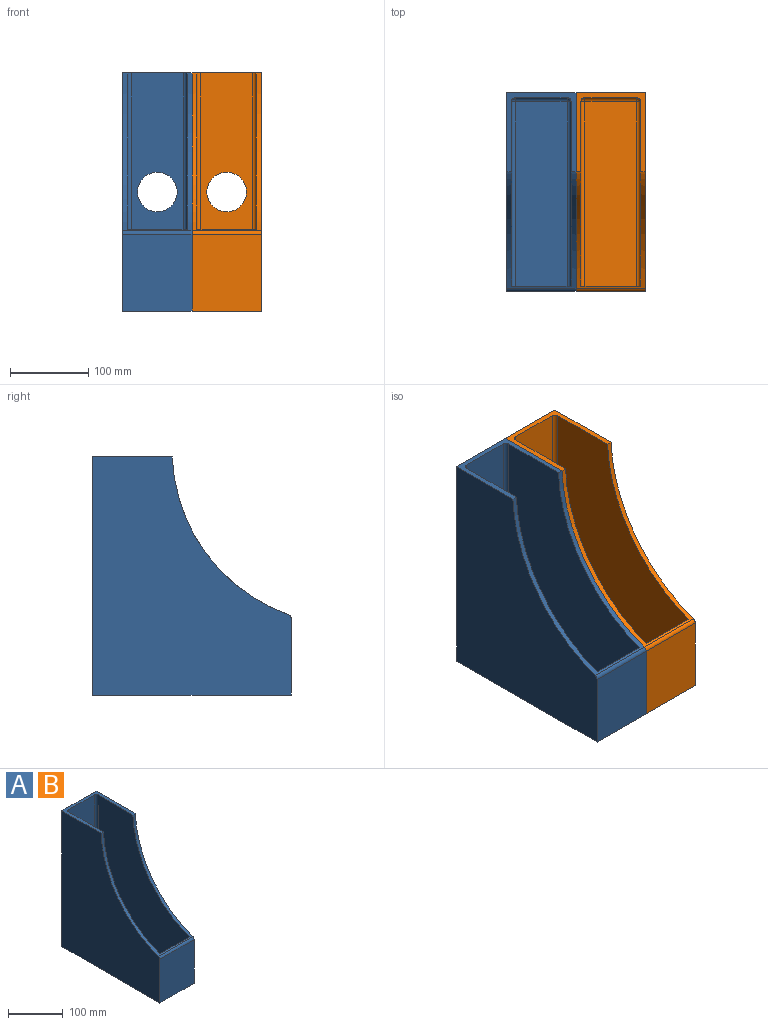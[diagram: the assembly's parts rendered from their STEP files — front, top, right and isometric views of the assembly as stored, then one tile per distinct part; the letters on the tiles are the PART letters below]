
ASSEMBLY  parts=2 mates=1
PART A: 21 faces, bbox 88.9x254x304.8 mm
  f0: cylinder r=224.76mm len=202.03mm, axis (-1,0,0), area 3624.3mm2, adj f4,f5,f6,f9,f10,f11,f19
  f1: plane 97.99x88.9mm, normal (0,-1,0), area 8711.2mm2, adj f2,f6,f11,f19
  f2: plane 254x88.9mm, normal (0,0,-1), area 22580.6mm2, adj f1,f3,f6,f11
  f3: plane 304.8x88.9mm, normal (0,1,0), area 25069.9mm2, adj f2,f4,f6,f11,f20
  f4: plane 101.6x88.9mm, normal (0,0,1), area 1785.3mm2, adj f0,f3,f5,f6,f7,f10,f11,f12
  f5: plane 293.37x236.22mm, normal (1,0,0), area 48315.3mm2, adj f0,f4,f9,f14,f15
  f6: plane 304.8x254mm, normal (-1,0,0), area 55149mm2, adj f0,f1,f2,f3,f4,f19
  f7: plane 293.37x66.04mm, normal (0,-1,0), area 17347.3mm2, adj f4,f12,f15,f18,f20
  f8: plane 236.22x66.04mm, normal (0,0,1), area 15600mm2, adj f9,f13,f14,f18
  f9: plane 97.51x76.2mm, normal (0,1,0), area 7419.1mm2, adj f0,f5,f8,f10,f13,f14
  f10: plane 293.37x236.22mm, normal (-1,0,0), area 48315.3mm2, adj f0,f4,f9,f12,f13
  f11: plane 304.8x254mm, normal (1,0,0), area 55149mm2, adj f0,f1,f2,f3,f4,f19
  f12: cylinder r=5.08mm len=293.37mm, axis (0,0,1), area 2341mm2, adj f4,f7,f10,f16
  f13: cylinder r=5.08mm len=236.22mm, axis (0,1,0), area 1885mm2, adj f8,f9,f10,f16
  f14: cylinder r=5.08mm len=236.22mm, axis (0,-1,0), area 1885mm2, adj f5,f8,f9,f17
  f15: cylinder r=5.08mm len=293.37mm, axis (0,0,-1), area 2341mm2, adj f4,f5,f7,f17
  f16: sphere r=5.08mm, area 40.5mm2, adj f12,f13,f18
  f17: sphere r=5.08mm, area 40.5mm2, adj f14,f15,f18
  f18: cylinder r=5.08mm len=66.04mm, axis (-1,0,0), area 527mm2, adj f7,f8,f16,f17
  f19: cylinder r=5.08mm len=88.9mm, axis (-1,0,0), area 554.6mm2, adj f0,f1,f6,f11
  f20: cylinder r=25.4mm len=50.8mm, axis (0,1,0), area 1013.4mm2, adj f3,f7
PART B: same geometry as A
PLACE A t=(-204.74,-3.34,13.5)mm
PLACE B t=(-115.84,-3.34,13.5)mm
MATE fastened A.f11 <-> B.f6  axis (1,0,0) through (-115.84,21.9,-50.53)mm
